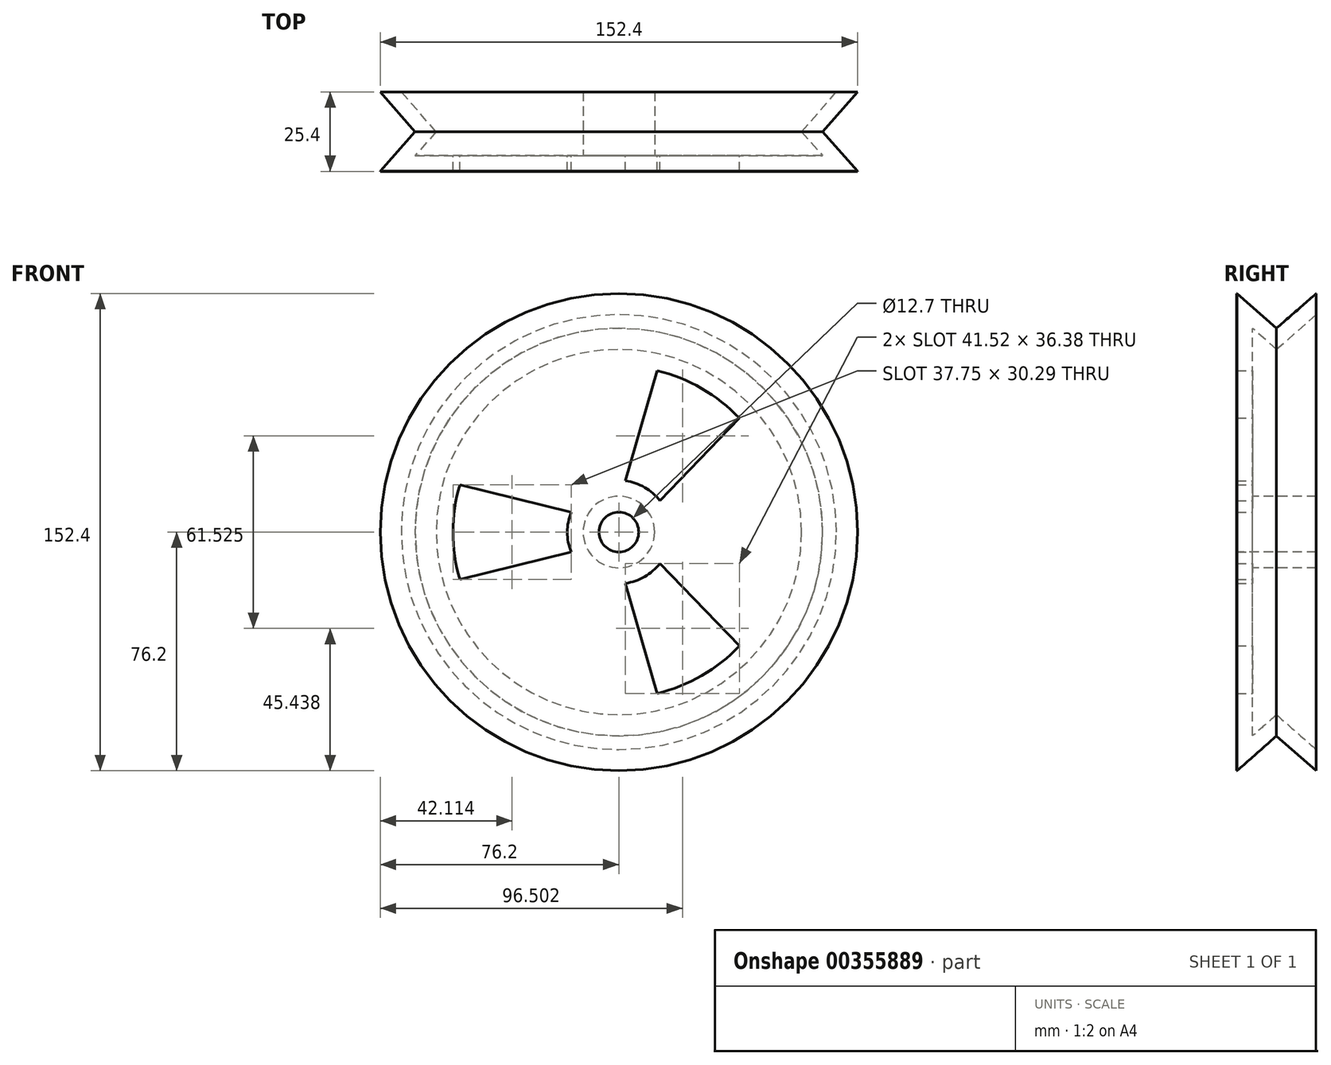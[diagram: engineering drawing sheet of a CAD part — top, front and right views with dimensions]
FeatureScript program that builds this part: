
annotation { "Feature Type Name" : "Feature", "Feature Type Description" : "" }
export const myFeature = defineFeature(function(context is Context, id is Id, definition is map)
    precondition{}
    {
        {
            var Q0;
            Q0=qCreatedBy(makeId("Front.planeOp"),FACE);
            var sketch = newSketch(context, id + "F0", { "sketchPlane" : qUnion([Q0])});
            skCircle(sketch, "E0", {"center": v(0, 0) * mm, "radius": 76.2 * mm});
            skSolve(sketch);
        }
        {
            var Q0;
            Q0=qSketchRegion(id+"F0",true);
            extrude(context, id + "F1", {"entities" : qUnion([Q0]), "depth" : 25.4 * mm});
        }
        {
            var Q0;
            Q0=qCreatedBy(makeId("Right.planeOp"),FACE);
            var sketch = newSketch(context, id + "F2", { "sketchPlane" : qUnion([Q0])});
            skLineSegment(sketch, "E1", {"start": v(0, 76.23) * mm, "end": v(-12.7, 76.23) * mm});
            skLineSegment(sketch, "E2", {"start": v(0, 76.23) * mm, "end": v(-12.7, 65.11) * mm});
            skLineSegment(sketch, "E3", {"start": v(-12.7, 65.11) * mm, "end": v(-25.3, 76.23) * mm});
            skLineSegment(sketch, "E4", {"start": v(-25.3, 76.23) * mm, "end": v(0, 76.23) * mm});
            skSolve(sketch);
        }
        {
            var Q0;
            Q0=qSketchRegion(id+"F2",true);
            var Q1;
            Q1=makeQuery(id+"F1.opExtrude","CAP_EDGE",EDGE,{"disambiguationData":[OSD([sQuery(id+"F0.wireOp",EDGE,"E0")])],"isStart":false});
            revolve(context, id + "F3", {"operationType" : NewBodyOperationType.REMOVE, "entities" : qUnion([Q0]), "axis" : qUnion([Q1]), "revolveType" : RevolveType.FULL, "oppositeDirection" : true});
        }
        {
            var Q0;
            Q0=makeQuery(id+"F1.opExtrude","CAP_FACE",FACE,{"disambiguationData":[OSD([sQuery(id+"F0.wireOp",EDGE,"E0")])],"isStart":false});
            var sketch = newSketch(context, id + "F4", { "sketchPlane" : qUnion([Q0])});
            skCircle(sketch, "E5", {"center": v(0, 0) * mm, "radius": 6.35 * mm});
            skSolve(sketch);
        }
        {
            var Q0;
            Q0=qSketchRegion(id+"F4",true);
            extrude(context, id + "F5", {"entities" : qUnion([Q0]), "operationType" : NewBodyOperationType.REMOVE, "oppositeDirection" : true, "depth" : 25.4 * mm});
        }
        {
            var Q0;
            Q0=makeQuery(id+"F1.opExtrude","CAP_FACE",FACE,{"disambiguationData":[OSD([sQuery(id+"F0.wireOp",EDGE,"E0")])],"isStart":true});
            shell(context, id + "F6", {"entities" : qUnion([Q0]), "thickness" : 5.08 * mm});
        }
        {
            var Q0;
            {var subQ0=sQuery(id+"F0.wireOp",EDGE,"E0");Q0=makeQuery(id+"F6.opShell","OFFSET_FACE",FACE,{"disambiguationData":[OSD([subQ0]),TDD([makeQuery(id+"F1.opExtrude","CAP_FACE",FACE,{"disambiguationData":[OSD([subQ0])],"isStart":false})])]});}
            var sketch = newSketch(context, id + "F7", { "sketchPlane" : qUnion([Q0])});
            skCircle(sketch, "E6", {"center": v(0, 0) * mm, "radius": 52.96 * mm});
            skCircle(sketch, "E7", {"center": v(0, 0) * mm, "radius": 16.48 * mm});
            skLineSegment(sketch, "E8", {"start": v(50.75, 15.15) * mm, "end": v(15.2, 6.34) * mm});
            skLineSegment(sketch, "E9.MirrorCS", {"start": v(50.75, -15.15) * mm, "end": v(15.2, -6.34) * mm});
            skPoint(sketch, "E10.start.orphan", {"position": v(16.48, 0) * mm});
            skLineSegment(sketch, "E11.1.0", {"start": v(-12.26, 51.52) * mm, "end": v(-2.11, 16.34) * mm});
            skLineSegment(sketch, "E11.1.1", {"start": v(-38.5, 36.38) * mm, "end": v(-13.1, 10) * mm});
            skLineSegment(sketch, "E11.2.0", {"start": v(-38.5, -36.38) * mm, "end": v(-13.1, -10) * mm});
            skLineSegment(sketch, "E11.2.1", {"start": v(-12.26, -51.52) * mm, "end": v(-2.11, -16.34) * mm});
            skSolve(sketch);
        }
        {
            var Q0;
            {var subQ0=sQuery(id+"F7.wireOp",EDGE,"E8");Q0=makeQuery(id+"F7.imprint","IMPRINT",FACE,{"disambiguationData":[TD([[makeQuery(id+"F7.imprint","IMPRINT",EDGE,{"derivedFrom":subQ0}),1.0]])]});}
            var Q1;
            {var subQ0=sQuery(id+"F7.wireOp",EDGE,"E11.2.0");Q1=makeQuery(id+"F7.imprint","IMPRINT",FACE,{"disambiguationData":[TD([[makeQuery(id+"F7.imprint","IMPRINT",EDGE,{"derivedFrom":subQ0}),-1.0]])]});}
            var Q2;
            {var subQ0=sQuery(id+"F7.wireOp",EDGE,"E11.1.0");Q2=makeQuery(id+"F7.imprint","IMPRINT",FACE,{"disambiguationData":[TD([[makeQuery(id+"F7.imprint","IMPRINT",EDGE,{"derivedFrom":subQ0}),-1.0]])]});}
            extrude(context, id + "F8", {"entities" : qUnion([Q0, Q1, Q2]), "operationType" : NewBodyOperationType.REMOVE, "endBound" : BoundingType.THROUGH_ALL, "oppositeDirection" : true, "depth" : 25.4 * mm});
        }
    });
